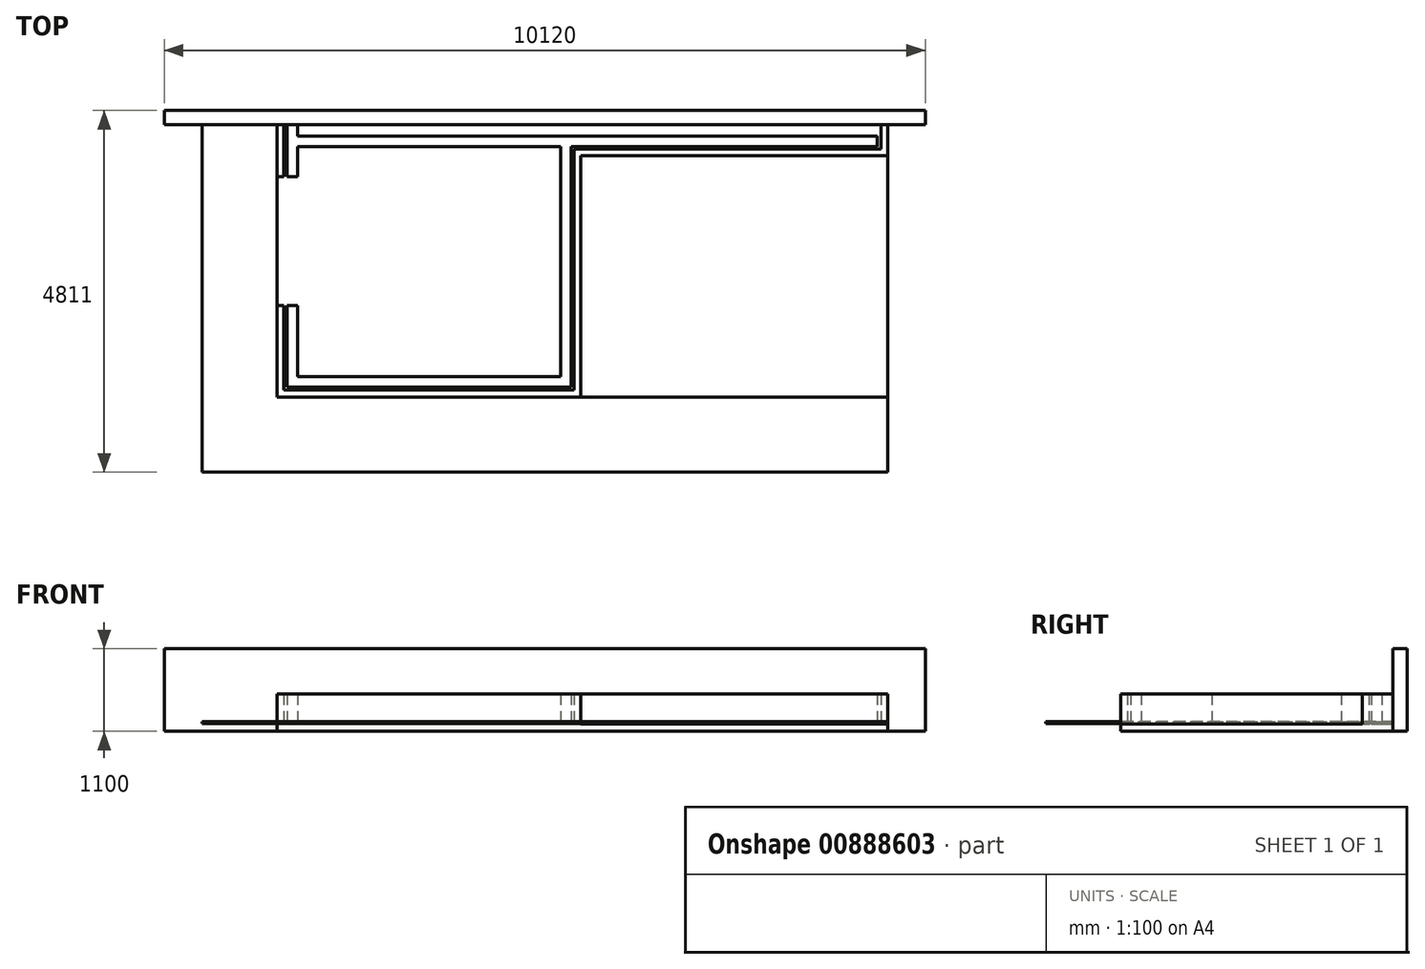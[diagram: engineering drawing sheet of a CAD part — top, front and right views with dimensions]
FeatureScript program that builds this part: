
annotation { "Feature Type Name" : "Feature", "Feature Type Description" : "" }
export const myFeature = defineFeature(function(context is Context, id is Id, definition is map)
    precondition{}
    {
        {
            var Q0;
            Q0=qCreatedBy(makeId("Top.planeOp"),FACE);
            var sketch = newSketch(context, id + "F0", { "sketchPlane" : qUnion([Q0])});
            skLineSegment(sketch, "E0.bottom", {"start": v(0, 0) * mm, "end": v(8120, 0) * mm});
            skLineSegment(sketch, "E0.top", {"start": v(0, 3621) * mm, "end": v(8120, 3621) * mm});
            skLineSegment(sketch, "E0.left", {"start": v(0, 0) * mm, "end": v(0, 3621) * mm});
            skLineSegment(sketch, "E0.right", {"start": v(8120, 0) * mm, "end": v(8120, 3621) * mm});
            skSolve(sketch);
        }
        {
            var Q0;
            Q0=makeQuery(id+"F0.imprint","IMPRINT",FACE,{"disambiguationData":[TD([[makeQuery(id+"F0.imprint","IMPRINT",EDGE,{"derivedFrom":sQuery(id+"F0.wireOp",EDGE,"E0.bottom")}),1.0]])]});
            var Q1;
            Q1=sQuery(id+"F0.wireOp",EDGE,"E0.left");
            var Q2;
            Q2=sQuery(id+"F0.wireOp",EDGE,"E0.top");
            var Q3;
            Q3=sQuery(id+"F0.wireOp",EDGE,"E0.right");
            var Q4;
            Q4=sQuery(id+"F0.wireOp",EDGE,"E0.bottom");
            extrude(context, id + "F1", {"entities" : qUnion([Q0]), "surfaceEntities" : qUnion([Q1, Q2, Q3, Q4]), "oppositeDirection" : true, "depth" : 100 * mm, "offsetDistance" : 25 * mm});
        }
        {
            var Q0;
            Q0=makeQuery(id+"F1.opExtrude","CAP_FACE",FACE,{"disambiguationData":[OSD([sQuery(id+"F0.wireOp",EDGE,"E0.bottom"),sQuery(id+"F0.wireOp",EDGE,"E0.top"),sQuery(id+"F0.wireOp",EDGE,"E0.left"),sQuery(id+"F0.wireOp",EDGE,"E0.right")])],"isStart":true});
            var sketch = newSketch(context, id + "F2", { "sketchPlane" : qUnion([Q0])});
            skLineSegment(sketch, "E1.bottom", {"start": v(0, 3621) * mm, "end": v(90, 3621) * mm});
            skLineSegment(sketch, "E1.top", {"start": v(0, 2930) * mm, "end": v(90, 2930) * mm});
            skLineSegment(sketch, "E1.left", {"start": v(0, 3621) * mm, "end": v(0, 2930) * mm});
            skLineSegment(sketch, "E1.right", {"start": v(90, 3621) * mm, "end": v(90, 2930) * mm});
            skLineSegment(sketch, "E2", {"start": v(0, 1214) * mm, "end": v(0, 0) * mm});
            skLineSegment(sketch, "E3", {"start": v(0, 0) * mm, "end": v(4040, 0) * mm});
            skLineSegment(sketch, "E4", {"start": v(4040, 0) * mm, "end": v(4040, 3211) * mm});
            skLineSegment(sketch, "E5", {"start": v(4040, 3211) * mm, "end": v(8120, 3211) * mm});
            skLineSegment(sketch, "E6", {"start": v(8120, 3211) * mm, "end": v(8120, 3621) * mm});
            skLineSegment(sketch, "E7", {"start": v(8120, 3621) * mm, "end": v(8030, 3621) * mm});
            skLineSegment(sketch, "E8", {"start": v(8030, 3621) * mm, "end": v(8030, 3301) * mm});
            skLineSegment(sketch, "E9", {"start": v(8030, 3301) * mm, "end": v(3950, 3301) * mm});
            skLineSegment(sketch, "E10", {"start": v(3950, 3301) * mm, "end": v(3950, 90) * mm});
            skLineSegment(sketch, "E11", {"start": v(3950, 90) * mm, "end": v(90, 90) * mm});
            skLineSegment(sketch, "E12", {"start": v(90, 90) * mm, "end": v(90, 1214) * mm});
            skLineSegment(sketch, "E13", {"start": v(90, 1214) * mm, "end": v(0, 1214) * mm});
            skLineSegment(sketch, "E14", {"start": v(1817.3, 90) * mm, "end": v(1817.3, 0) * mm, "construction": true});
            skLineSegment(sketch, "E15", {"start": v(3950, 1283.64) * mm, "end": v(4040, 1283.64) * mm, "construction": true});
            skLineSegment(sketch, "E16", {"start": v(5345.82, 3211) * mm, "end": v(5345.82, 3301) * mm, "construction": true});
            skLineSegment(sketch, "E17", {"start": v(130, 3621) * mm, "end": v(130, 2930) * mm});
            skLineSegment(sketch, "E18", {"start": v(130, 2930) * mm, "end": v(270, 2930) * mm});
            skLineSegment(sketch, "E19", {"start": v(270, 2930) * mm, "end": v(270, 3330) * mm});
            skLineSegment(sketch, "E20", {"start": v(270, 3330) * mm, "end": v(3770, 3330) * mm});
            skLineSegment(sketch, "E21", {"start": v(3770, 3330) * mm, "end": v(3770, 270) * mm});
            skLineSegment(sketch, "E22", {"start": v(3770, 270) * mm, "end": v(270, 270) * mm});
            skLineSegment(sketch, "E23", {"start": v(270, 270) * mm, "end": v(270, 1214) * mm});
            skLineSegment(sketch, "E24", {"start": v(270, 1214) * mm, "end": v(130, 1214) * mm});
            skLineSegment(sketch, "E25", {"start": v(130, 1214) * mm, "end": v(130, 130) * mm});
            skLineSegment(sketch, "E26", {"start": v(130, 130) * mm, "end": v(3910, 130) * mm});
            skLineSegment(sketch, "E27", {"start": v(3910, 130) * mm, "end": v(3910, 3330) * mm});
            skLineSegment(sketch, "E28", {"start": v(3910, 3330) * mm, "end": v(7980, 3330) * mm});
            skLineSegment(sketch, "E29", {"start": v(7980, 3330) * mm, "end": v(7980, 3470) * mm});
            skLineSegment(sketch, "E30", {"start": v(7980, 3470) * mm, "end": v(270, 3470) * mm});
            skLineSegment(sketch, "E31", {"start": v(270, 3470) * mm, "end": v(270, 3621) * mm});
            skLineSegment(sketch, "E32", {"start": v(270, 3621) * mm, "end": v(130, 3621) * mm});
            skLineSegment(sketch, "E33", {"start": v(2329.99, 130) * mm, "end": v(2329.99, 270) * mm, "construction": true});
            skLineSegment(sketch, "E34", {"start": v(3770, 1385.03) * mm, "end": v(3910, 1385.03) * mm, "construction": true});
            skSolve(sketch);
        }
        {
            var Q0;
            Q0=makeQuery(id+"F2.imprint","IMPRINT",FACE,{"disambiguationData":[TD([[makeQuery(id+"F2.imprint","IMPRINT",EDGE,{"derivedFrom":sQuery(id+"F2.wireOp",EDGE,"E1.bottom")}),-1.0]])]});
            var Q1;
            Q1=makeQuery(id+"F2.imprint","IMPRINT",FACE,{"disambiguationData":[TD([[makeQuery(id+"F2.imprint","IMPRINT",EDGE,{"derivedFrom":sQuery(id+"F2.wireOp",EDGE,"E17")}),1.0]])]});
            var Q2;
            Q2=makeQuery(id+"F2.imprint","IMPRINT",FACE,{"disambiguationData":[TD([[makeQuery(id+"F2.imprint","IMPRINT",EDGE,{"derivedFrom":sQuery(id+"F2.wireOp",EDGE,"E2")}),-1.0]])]});
            extrude(context, id + "F3", {"entities" : qUnion([Q0, Q1, Q2]), "operationType" : NewBodyOperationType.ADD, "depth" : 400 * mm, "offsetDistance" : 25 * mm});
        }
        {
            var Q0;
            Q0=makeQuery(id+"F3.opExtrude","CAP_FACE",FACE,{"disambiguationData":[OSD([sQuery(id+"F2.wireOp",EDGE,"E17"),sQuery(id+"F2.wireOp",EDGE,"E18"),sQuery(id+"F2.wireOp",EDGE,"E19"),sQuery(id+"F2.wireOp",EDGE,"E20"),sQuery(id+"F2.wireOp",EDGE,"E21"),sQuery(id+"F2.wireOp",EDGE,"E22"),sQuery(id+"F2.wireOp",EDGE,"E23"),sQuery(id+"F2.wireOp",EDGE,"E24"),sQuery(id+"F2.wireOp",EDGE,"E25"),sQuery(id+"F2.wireOp",EDGE,"E26"),sQuery(id+"F2.wireOp",EDGE,"E27"),sQuery(id+"F2.wireOp",EDGE,"E28"),sQuery(id+"F2.wireOp",EDGE,"E29"),sQuery(id+"F2.wireOp",EDGE,"E30"),sQuery(id+"F2.wireOp",EDGE,"E31"),sQuery(id+"F2.wireOp",EDGE,"E32")])],"isStart":false});
            cPlane(context, id + "F4", {"entities" : qUnion([Q0]), "cplaneType" : CPlaneType.OFFSET, "offset" : 370 * mm, "oppositeDirection" : true, "width" : 150 * mm, "height" : 150 * mm});
        }
        {
            var Q0;
            Q0=qCreatedBy(id+"F4.planeOp",FACE);
            var sketch = newSketch(context, id + "F5", { "sketchPlane" : qUnion([Q0])});
            skLineSegment(sketch, "E35", {"start": v(0, 3621) * mm, "end": v(-1000, 3621) * mm});
            skLineSegment(sketch, "E36", {"start": v(-1000, 3621) * mm, "end": v(-1000, -1000) * mm});
            skLineSegment(sketch, "E37", {"start": v(-1000, -1000) * mm, "end": v(8120, -1000) * mm});
            skLineSegment(sketch, "E38", {"start": v(8120, -1000) * mm, "end": v(8120, 0) * mm});
            skLineSegment(sketch, "E39", {"start": v(8120, 0) * mm, "end": v(0, 0) * mm});
            skLineSegment(sketch, "E40", {"start": v(0, 0) * mm, "end": v(0, 3621) * mm});
            skSolve(sketch);
        }
        {
            var Q0;
            Q0=makeQuery(id+"F5.imprint","IMPRINT",FACE,{"disambiguationData":[TD([[makeQuery(id+"F5.imprint","IMPRINT",EDGE,{"derivedFrom":sQuery(id+"F5.wireOp",EDGE,"E35")}),1.0]])]});
            extrude(context, id + "F6", {"entities" : qUnion([Q0]), "operationType" : NewBodyOperationType.ADD, "oppositeDirection" : true, "depth" : 25 * mm, "offsetDistance" : 25 * mm});
        }
        {
            var Q0;
            {var subQ0=sQuery(id+"F0.wireOp",EDGE,"E0.left");var subQ1=sQuery(id+"F0.wireOp",EDGE,"E0.top");Q0=makeQuery(id+"F3.boolean.opBoolean","SPLIT",FACE,{"disambiguationData":[TD([makeQuery(id+"F1.opExtrude","SWEPT_FACE",FACE,{"disambiguationData":[OSD([subQ1])]})])],"derivedFrom":makeQuery(id+"F1.opExtrude","CAP_FACE",FACE,{"disambiguationData":[OSD([sQuery(id+"F0.wireOp",EDGE,"E0.bottom"),subQ1,subQ0,sQuery(id+"F0.wireOp",EDGE,"E0.right")])],"isStart":true})});}
            var sketch = newSketch(context, id + "F7", { "sketchPlane" : qUnion([Q0])});
            skLineSegment(sketch, "E41.bottom", {"start": v(-1500, 3621) * mm, "end": v(8620, 3621) * mm});
            skLineSegment(sketch, "E41.top", {"start": v(-1500, 3811) * mm, "end": v(8620, 3811) * mm});
            skLineSegment(sketch, "E41.left", {"start": v(-1500, 3621) * mm, "end": v(-1500, 3811) * mm});
            skLineSegment(sketch, "E41.right", {"start": v(8620, 3621) * mm, "end": v(8620, 3811) * mm});
            skSolve(sketch);
        }
        {
            var Q0;
            Q0=makeQuery(id+"F7.imprint","IMPRINT",FACE,{"disambiguationData":[TD([[makeQuery(id+"F7.imprint","IMPRINT",EDGE,{"derivedFrom":sQuery(id+"F7.wireOp",EDGE,"E41.top")}),-1.0]])]});
            extrude(context, id + "F8", {"entities" : qUnion([Q0]), "operationType" : NewBodyOperationType.ADD, "depth" : 1000 * mm, "offsetDistance" : 25 * mm, "hasSecondDirection" : true, "secondDirectionOppositeDirection" : true, "secondDirectionDepth" : 100 * mm});
        }
    });
